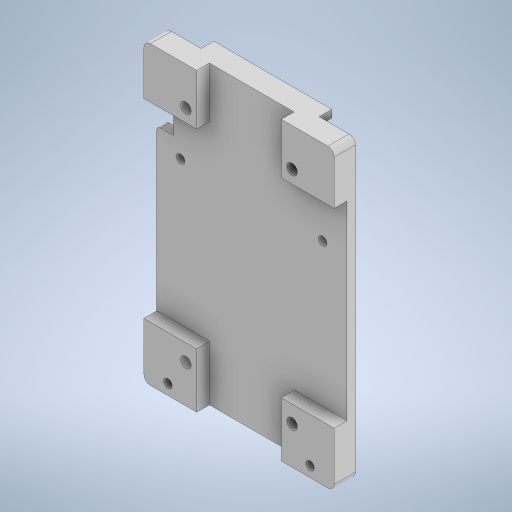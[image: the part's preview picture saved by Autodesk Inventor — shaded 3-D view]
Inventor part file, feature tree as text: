
AUTODESK INVENTOR PART (.ipt)
format: ipt  version: 2023 (Build 270158000, 158)  size: 360,960 bytes
history: native  units: mm
features: sketch x6, extrude x6, projected_geometry x4, other x1, hole x1, fillet x1
ambient origin geometry x8: Origin, YZ Plane, XZ Plane, XY Plane, X Axis, Y Axis, Z Axis, Center Point
bodies: Body1 (feature_tree)
feature tree (19):
  other  "솔리드1"
  sketch  "스케치1"
  extrude  "돌출1"  Depth=45.0mm
  extrude  "돌출2"  Depth=70.0mm
  sketch  "스케치3"
  extrude  "돌출3"  Depth=25.1mm
  extrude  "돌출4"  Depth=52.1mm
  extrude  "돌출6"  Depth=2.5mm
  hole  "구멍3"  [1 undecoded]
  extrude  "돌출7"  Depth=12.0mm
  fillet  "모깎기1"  Radius=13.0mm
  sketch  "스케치4"
  sketch  "스케치5"
  sketch  "스케치7"
  projected_geometry  "투영된 루프4"
  projected_geometry  "투영된 루프5"
  projected_geometry  "투영된 루프6"
  projected_geometry  "투영된 루프7"
  sketch  "스케치9"
note: 1 required parameter value undecoded (feature->parameter linkage not recoverable at this tier; creation-order binding heuristic only, values carry confidence <= 0.55)
